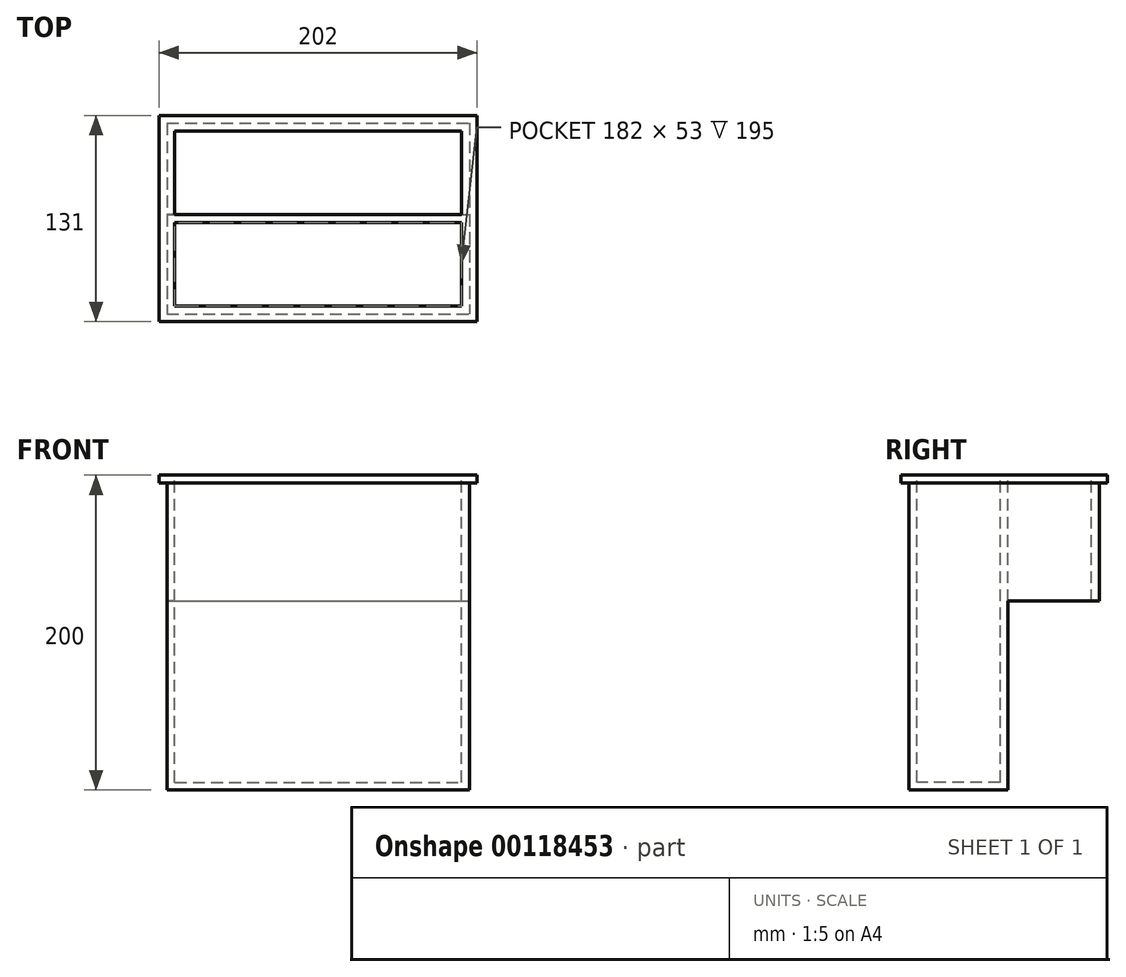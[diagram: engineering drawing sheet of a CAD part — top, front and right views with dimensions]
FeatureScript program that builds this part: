
annotation { "Feature Type Name" : "Feature", "Feature Type Description" : "" }
export const myFeature = defineFeature(function(context is Context, id is Id, definition is map)
    precondition{}
    {
        {
            var Q0;
            Q0=qCreatedBy(makeId("Top.planeOp"),FACE);
            var sketch = newSketch(context, id + "F0", { "sketchPlane" : qUnion([Q0])});
            skLineSegment(sketch, "E0.bottom", {"start": v(-100.1, 49.43) * mm, "end": v(81.9, 49.43) * mm});
            skLineSegment(sketch, "E0.top", {"start": v(-100.1, -3.57) * mm, "end": v(81.9, -3.57) * mm});
            skLineSegment(sketch, "E0.left", {"start": v(-100.1, 49.43) * mm, "end": v(-100.1, -3.57) * mm});
            skLineSegment(sketch, "E0.right", {"start": v(81.9, 49.43) * mm, "end": v(81.9, -3.57) * mm});
            skLineSegment(sketch, "E1.bottom", {"start": v(-105.1, 54.43) * mm, "end": v(86.9, 54.43) * mm});
            skLineSegment(sketch, "E1.top", {"start": v(-105.1, -66.57) * mm, "end": v(86.9, -66.57) * mm});
            skLineSegment(sketch, "E1.left", {"start": v(-105.1, 54.43) * mm, "end": v(-105.1, -66.57) * mm});
            skLineSegment(sketch, "E1.right", {"start": v(86.9, 54.43) * mm, "end": v(86.9, -66.57) * mm});
            skLineSegment(sketch, "E2.bottom", {"start": v(-100.1, -8.57) * mm, "end": v(81.9, -8.57) * mm});
            skLineSegment(sketch, "E2.top", {"start": v(-100.1, -61.57) * mm, "end": v(81.9, -61.57) * mm});
            skLineSegment(sketch, "E2.left", {"start": v(-100.1, -8.57) * mm, "end": v(-100.1, -61.57) * mm});
            skLineSegment(sketch, "E2.right", {"start": v(81.9, -8.57) * mm, "end": v(81.9, -61.57) * mm});
            skLineSegment(sketch, "E3", {"start": v(-100.1, -3.57) * mm, "end": v(-100.1, -8.57) * mm, "construction": true});
            skLineSegment(sketch, "E4", {"start": v(-88.11, 49.43) * mm, "end": v(-88.11, 54.43) * mm, "construction": true});
            skLineSegment(sketch, "E5", {"start": v(-100.1, 35.8) * mm, "end": v(-105.1, 35.8) * mm, "construction": true});
            skLineSegment(sketch, "E6", {"start": v(81.9, 41.52) * mm, "end": v(86.9, 41.52) * mm, "construction": true});
            skLineSegment(sketch, "E7", {"start": v(-50.62, -61.57) * mm, "end": v(-50.62, -66.57) * mm, "construction": true});
            skLineSegment(sketch, "E8", {"start": v(-100.1, -3.57) * mm, "end": v(-105.1, -3.57) * mm});
            skLineSegment(sketch, "E9", {"start": v(81.9, -3.57) * mm, "end": v(86.9, -3.57) * mm});
            skLineSegment(sketch, "E10.bottom", {"start": v(-110.1, 59.43) * mm, "end": v(91.9, 59.43) * mm});
            skLineSegment(sketch, "E10.top", {"start": v(-110.1, -71.57) * mm, "end": v(91.9, -71.57) * mm});
            skLineSegment(sketch, "E10.left", {"start": v(-110.1, 59.43) * mm, "end": v(-110.1, -71.57) * mm});
            skLineSegment(sketch, "E10.right", {"start": v(91.9, 59.43) * mm, "end": v(91.9, -71.57) * mm});
            skLineSegment(sketch, "E11", {"start": v(86.9, 48.22) * mm, "end": v(91.9, 48.22) * mm, "construction": true});
            skLineSegment(sketch, "E12", {"start": v(69.45, 54.43) * mm, "end": v(69.45, 59.43) * mm, "construction": true});
            skLineSegment(sketch, "E13", {"start": v(10.58, -66.57) * mm, "end": v(10.58, -71.57) * mm, "construction": true});
            skLineSegment(sketch, "E14", {"start": v(-105.1, -26.6) * mm, "end": v(-110.1, -26.6) * mm, "construction": true});
            skSolve(sketch);
        }
        {
            var Q0;
            Q0=makeQuery(id+"F0.imprint","IMPRINT",FACE,{"disambiguationData":[TD([[makeQuery(id+"F0.imprint","IMPRINT",EDGE,{"derivedFrom":sQuery(id+"F0.wireOp",EDGE,"E0.top")}),-1.0]])]});
            extrude(context, id + "F1", {"entities" : qUnion([Q0]), "oppositeDirection" : true, "depth" : 200 * mm});
        }
        {
            var Q0;
            Q0=makeQuery(id+"F0.imprint","IMPRINT",FACE,{"disambiguationData":[TD([[makeQuery(id+"F0.imprint","IMPRINT",EDGE,{"derivedFrom":sQuery(id+"F0.wireOp",EDGE,"E0.bottom")}),1.0]])]});
            extrude(context, id + "F2", {"entities" : qUnion([Q0]), "operationType" : NewBodyOperationType.ADD, "oppositeDirection" : true, "depth" : 80 * mm});
        }
        {
            var Q0;
            Q0=makeQuery(id+"F1.opExtrude","CAP_FACE",FACE,{"disambiguationData":[OSD([sQuery(id+"F0.wireOp",EDGE,"E0.top"),sQuery(id+"F0.wireOp",EDGE,"E1.top"),sQuery(id+"F0.wireOp",EDGE,"E1.left"),sQuery(id+"F0.wireOp",EDGE,"E1.right"),sQuery(id+"F0.wireOp",EDGE,"E2.bottom"),sQuery(id+"F0.wireOp",EDGE,"E2.top"),sQuery(id+"F0.wireOp",EDGE,"E2.left"),sQuery(id+"F0.wireOp",EDGE,"E2.right"),sQuery(id+"F0.wireOp",EDGE,"E8"),sQuery(id+"F0.wireOp",EDGE,"E9")])],"isStart":false});
            var sketch = newSketch(context, id + "F3", { "sketchPlane" : qUnion([Q0])});
            skLineSegment(sketch, "E15.bottom", {"start": v(81.9, 8.57) * mm, "end": v(-100.1, 8.57) * mm});
            skLineSegment(sketch, "E15.top", {"start": v(81.9, 61.57) * mm, "end": v(-100.1, 61.57) * mm});
            skLineSegment(sketch, "E15.left", {"start": v(81.9, 8.57) * mm, "end": v(81.9, 61.57) * mm});
            skLineSegment(sketch, "E15.right", {"start": v(-100.1, 8.57) * mm, "end": v(-100.1, 61.57) * mm});
            skSolve(sketch);
        }
        {
            var Q0;
            Q0 = qSketchRegion(id + "F3", true);
            extrude(context, id + "F4", {"entities" : qUnion([Q0]), "operationType" : NewBodyOperationType.ADD, "oppositeDirection" : true, "depth" : 5 * mm});
        }
        {
            var Q0;
            {var subQ3=sQuery(id+"F0.wireOp",EDGE,"E1.bottom");Q0=makeQuery(id+"F0.imprint","IMPRINT",FACE,{"disambiguationData":[TD([[makeQuery(id+"F0.imprint","IMPRINT",EDGE,{"derivedFrom":subQ3}),1.0]])]});}
            extrude(context, id + "F5", {"entities" : qUnion([Q0]), "operationType" : NewBodyOperationType.ADD, "oppositeDirection" : true, "depth" : 5 * mm});
        }
    });
